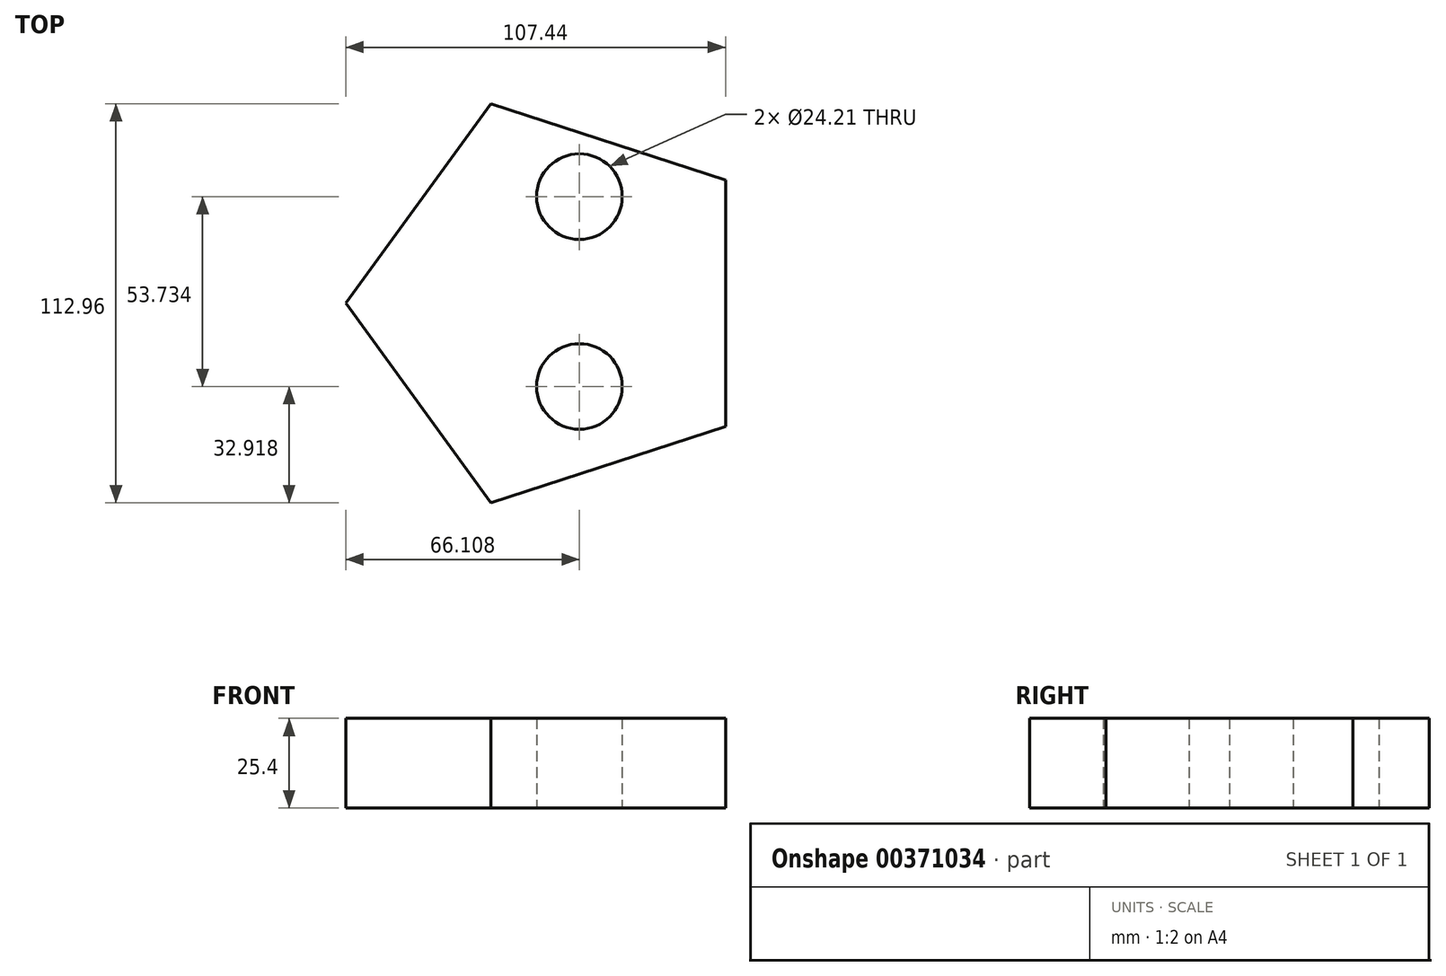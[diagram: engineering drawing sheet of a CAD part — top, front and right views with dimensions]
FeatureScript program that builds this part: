
annotation { "Feature Type Name" : "Feature", "Feature Type Description" : "" }
export const myFeature = defineFeature(function(context is Context, id is Id, definition is map)
    precondition{}
    {
        {
            var Q0;
            Q0=qCreatedBy(makeId("Top.planeOp"),FACE);
            var sketch = newSketch(context, id + "F0", { "sketchPlane" : qUnion([Q0])});
            skCircle(sketch, "E0.cCircle", {"center": v(0, 0) * mm, "radius": 48.05 * mm, "construction": true});
            skLineSegment(sketch, "E0.0", {"start": v(48.05, 34.9) * mm, "end": v(48.05, -34.9) * mm});
            skLineSegment(sketch, "E0.1", {"start": v(48.05, -34.9) * mm, "end": v(-18.35, -56.48) * mm});
            skLineSegment(sketch, "E0.2", {"start": v(-18.35, -56.48) * mm, "end": v(-59.39, 0) * mm});
            skLineSegment(sketch, "E0.3", {"start": v(-59.39, 0) * mm, "end": v(-18.35, 56.48) * mm});
            skLineSegment(sketch, "E0.4", {"start": v(-18.35, 56.48) * mm, "end": v(48.05, 34.9) * mm});
            skPoint(sketch, "E0.0.midPoint", {"position": v(48.05, 0) * mm});
            skSolve(sketch);
        }
        {
            var Q0;
            Q0 = qSketchRegion(id + "F0", true);
            extrude(context, id + "F1", {"entities" : qUnion([Q0]), "depth" : 25.4 * mm});
        }
        {
            var Q0;
            Q0=makeQuery(id+"F1.opExtrude","CAP_FACE",FACE,{"disambiguationData":[OSD([sQuery(id+"F0.wireOp",EDGE,"E0.0"),sQuery(id+"F0.wireOp",EDGE,"E0.1"),sQuery(id+"F0.wireOp",EDGE,"E0.2"),sQuery(id+"F0.wireOp",EDGE,"E0.3"),sQuery(id+"F0.wireOp",EDGE,"E0.4")])],"isStart":true});
            var sketch = newSketch(context, id + "F2", { "sketchPlane" : qUnion([Q0])});
            skPoint(sketch, "E1", {"position": v(0, 0) * mm});
            skPoint(sketch, "E2", {"position": v(6.72, 23.56) * mm});
            skPoint(sketch, "E3", {"position": v(6.72, -30.17) * mm});
            skSolve(sketch);
        }
        {
            var Q0;
            Q0=sQuery(id+"F2.wireOp",VERTEX,"E2");
            var Q1;
            Q1=sQuery(id+"F2.wireOp",VERTEX,"E3");
            var Q2;
            Q2=makeQuery(id+"F1.opExtrude","SWEPT_BODY",BODY,{"disambiguationData":[OSD([sQuery(id+"F0.wireOp",EDGE,"E0.0"),sQuery(id+"F0.wireOp",EDGE,"E0.1"),sQuery(id+"F0.wireOp",EDGE,"E0.2"),sQuery(id+"F0.wireOp",EDGE,"E0.3"),sQuery(id+"F0.wireOp",EDGE,"E0.4")])]});
            hole(context, id + "F3", {"style" : HoleStyle.SIMPLE, "endStyle" : HoleEndStyle.THROUGH, "standardTappedOrClearance" : lookupTablePath({ "standard" : "ANSI", "engagement" : "75%", "pitch" : "20 tpi", "size" : "1", "type" : "Tapped" }), "standardBlindInLast" : lookupTablePath({ "standard" : "ANSI", "engagement" : "75%", "pitch" : "20 tpi", "size" : "1", "type" : "Tapped" }), "holeDiameter" : 24.2 * mm, "showTappedDepth" : true, "isTappedThrough" : true, "tappedDepth" : 12.7 * mm, "tapClearance" : 3, "locations" : qUnion([Q0, Q1]), "scope" : qUnion([Q2]), "majorDiameter" : 25.4 * mm});
        }
    });
